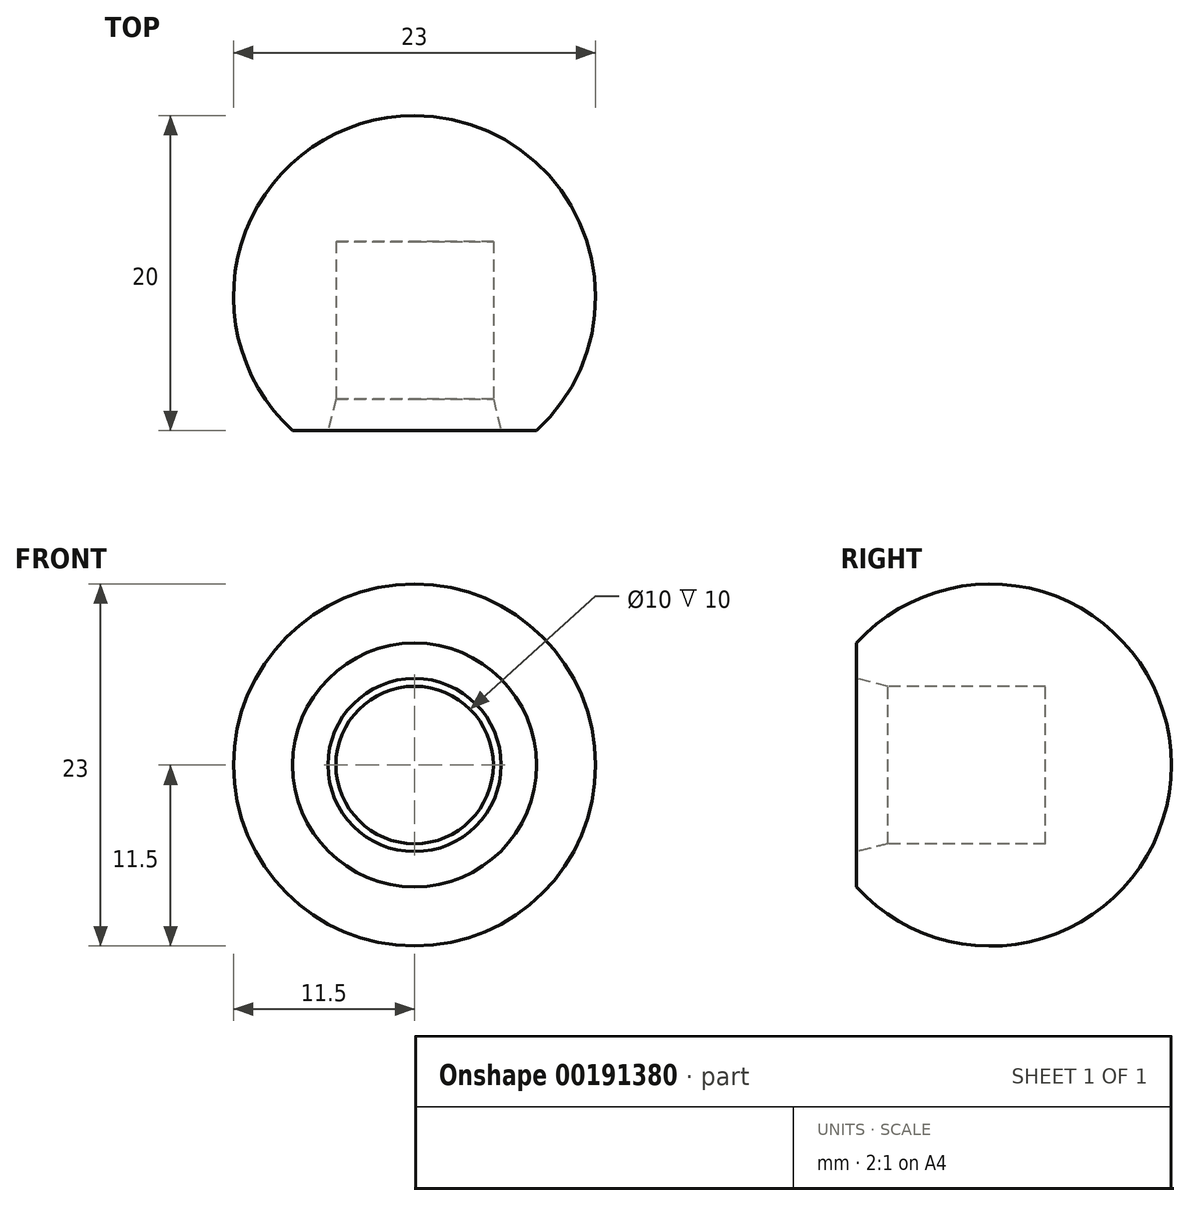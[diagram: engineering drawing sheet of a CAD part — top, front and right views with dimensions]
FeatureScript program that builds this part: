
annotation { "Feature Type Name" : "Feature", "Feature Type Description" : "" }
export const myFeature = defineFeature(function(context is Context, id is Id, definition is map)
    precondition{}
    {
        {
            var Q0;
            Q0=qCreatedBy(makeId("Top.planeOp"),FACE);
            var sketch = newSketch(context, id + "F0", { "sketchPlane" : qUnion([Q0])});
            skCircle(sketch, "E0", {"center": v(0, 0) * mm, "radius": 11.5 * mm});
            skLineSegment(sketch, "E1", {"start": v(0, 54.7) * mm, "end": v(0, -65.52) * mm});
            skPoint(sketch, "E2", {"position": v(0, -11.5) * mm});
            skSolve(sketch);
        }
        {
            var Q0;
            {var subQ0=sQuery(id+"F0.wireOp",EDGE,"E1");var subQ1=sQuery(id+"F0.wireOp",EDGE,"E0");var subQ2=makeQuery(id+"F0.imprint","INTERSECT",VERTEX,{"disambiguationData":[OD(0.0)],"derivedFrom":[subQ1,subQ0]});Q0=makeQuery(id+"F0.imprint","IMPRINT",FACE,{"disambiguationData":[TD([[makeQuery(id+"F0.imprint","IMPRINT",EDGE,{"disambiguationData":[TD([[subQ2,-1.0]])],"derivedFrom":subQ1}),1.0]])]});}
            var Q1;
            Q1=sQuery(id+"F0.wireOp",EDGE,"E0");
            var Q2;
            Q2=sQuery(id+"F0.wireOp",EDGE,"E1");
            revolve(context, id + "F1", {"entities" : qUnion([Q0]), "surfaceEntities" : qUnion([Q1]), "axis" : qUnion([Q2]), "revolveType" : RevolveType.FULL});
        }
        {
            var Q0;
            Q0=sQuery(id+"F0.wireOp",VERTEX,"E2");
            var Q1;
            Q1=sQuery(id+"F0.wireOp",EDGE,"E1");
            cPlane(context, id + "F2", {"entities" : qUnion([Q0, Q1]), "cplaneType" : CPlaneType.LINE_POINT, "offset" : 25 * mm, "width" : 150 * mm, "height" : 150 * mm});
        }
        {
            var Q0;
            Q0=qCreatedBy(id+"F2.planeOp",FACE);
            var sketch = newSketch(context, id + "F3", { "sketchPlane" : qUnion([Q0])});
            skCircle(sketch, "E3", {"center": v(0, 0) * mm, "radius": 5 * mm});
            skSolve(sketch);
        }
        {
            var Q0;
            Q0 = qSketchRegion(id + "F3", true);
            extrude(context, id + "F4", {"entities" : qUnion([Q0]), "operationType" : NewBodyOperationType.REMOVE, "oppositeDirection" : true, "depth" : 15 * mm});
        }
        {
            var Q0;
            Q0=qCreatedBy(id+"F2.planeOp",FACE);
            var sketch = newSketch(context, id + "F5", { "sketchPlane" : qUnion([Q0])});
            skCircle(sketch, "E4", {"center": v(0, 0) * mm, "radius": 8.3 * mm});
            skSolve(sketch);
        }
        {
            var Q0;
            Q0 = qSketchRegion(id + "F5", true);
            extrude(context, id + "F6", {"entities" : qUnion([Q0]), "operationType" : NewBodyOperationType.REMOVE, "oppositeDirection" : true, "depth" : 3 * mm});
        }
        {
            var Q0;
            Q0=makeQuery(id+"F6.boolean.opBoolean","INTERSECT",EDGE,{"derivedFrom":[makeQuery(id+"F4.boolean.opBoolean","COPY",FACE,{"derivedFrom":makeQuery(id+"F4.opExtrude","SWEPT_FACE",FACE,{"disambiguationData":[OSD([sQuery(id+"F3.wireOp",EDGE,"E3")])]})}),makeQuery(id+"F6.opExtrude","CAP_FACE",FACE,{"disambiguationData":[OSD([sQuery(id+"F5.wireOp",EDGE,"E4")])],"isStart":false})]});
            chamfer(context, id + "F7", {"entities" : qUnion([Q0]), "chamferType" : ChamferType.TWO_OFFSETS, "width1" : .5 * mm, "oppositeDirection" : false, "width2" : 2 * mm, "tangentPropagation" : true});
        }
    });
